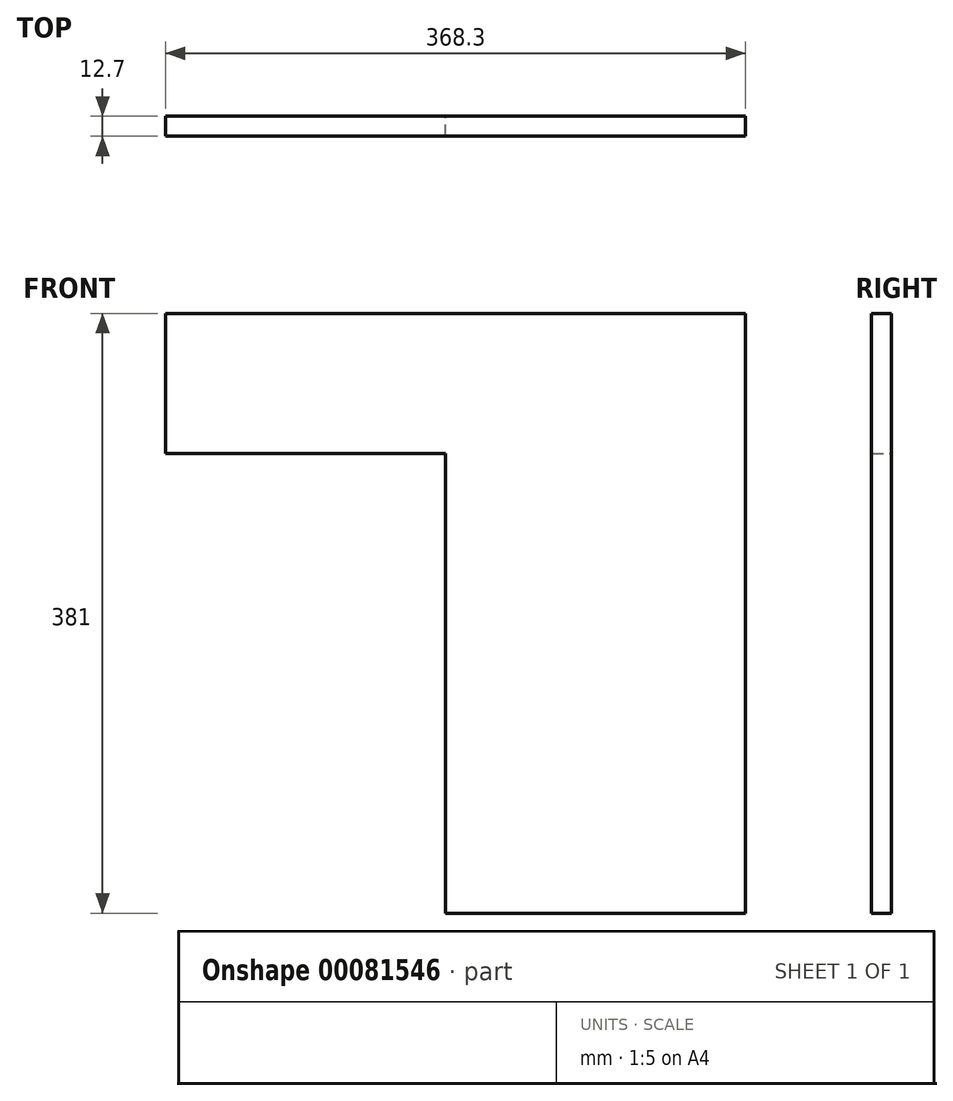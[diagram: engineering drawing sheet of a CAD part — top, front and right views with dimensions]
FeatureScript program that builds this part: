
annotation { "Feature Type Name" : "Feature", "Feature Type Description" : "" }
export const myFeature = defineFeature(function(context is Context, id is Id, definition is map)
    precondition{}
    {
        {
            var Q0;
            Q0=qCreatedBy(makeId("Front.planeOp"),FACE);
            var sketch = newSketch(context, id + "F0", { "sketchPlane" : qUnion([Q0])});
            skLineSegment(sketch, "E0.bottom", {"start": v(95.25, 190.5) * mm, "end": v(-95.25, 190.5) * mm});
            skLineSegment(sketch, "E0.top", {"start": v(95.25, -190.5) * mm, "end": v(-95.25, -190.5) * mm});
            skLineSegment(sketch, "E0.left", {"start": v(95.25, 190.5) * mm, "end": v(95.25, -190.5) * mm});
            skLineSegment(sketch, "E0.right", {"start": v(-95.25, 101.6) * mm, "end": v(-95.25, -190.5) * mm});
            skPoint(sketch, "E0.middle", {"position": v(0, 0) * mm});
            skLineSegment(sketch, "E1.bottom", {"start": v(-95.25, 190.5) * mm, "end": v(-273.05, 190.5) * mm});
            skLineSegment(sketch, "E1.top", {"start": v(-95.25, 101.6) * mm, "end": v(-273.05, 101.6) * mm});
            skLineSegment(sketch, "E1.right", {"start": v(-273.05, 190.5) * mm, "end": v(-273.05, 101.6) * mm});
            skSolve(sketch);
        }
        {
            var Q0;
            Q0 = qSketchRegion(id + "F0", true);
            extrude(context, id + "F1", {"entities" : qUnion([Q0]), "depth" : 12.7 * mm});
        }
    });
